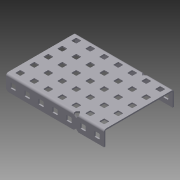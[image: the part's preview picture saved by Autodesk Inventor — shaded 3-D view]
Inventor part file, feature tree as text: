
AUTODESK INVENTOR PART (.ipt)
format: ipt  version: 2014 SP1 (Build 180222100, 222)  size: 1,121,280 bytes
history: native  units: in
note: dims shown in document units (in); Inventor stores cm internally (conversion verified against a paired STEP export)
features: other x1, imported_body x1, extrude x1, sketch x1
ambient origin geometry x8: Origin, YZ Plane, XZ Plane, XY Plane, X Axis, Y Axis, Z Axis, Center Point
bodies: Body1 (feature_tree)
feature tree (4):
  parser-record x1  (decoder bookkeeping rows leaked as tree rows — omitted from the tree; the rows remain in map.json)
  imported_body  "Base1"
  extrude  "Extrusion1"  Depth=3.5in
  sketch  "Sketch1"  dims[d0=1.0in d1=0.0in d2=3.5in]
